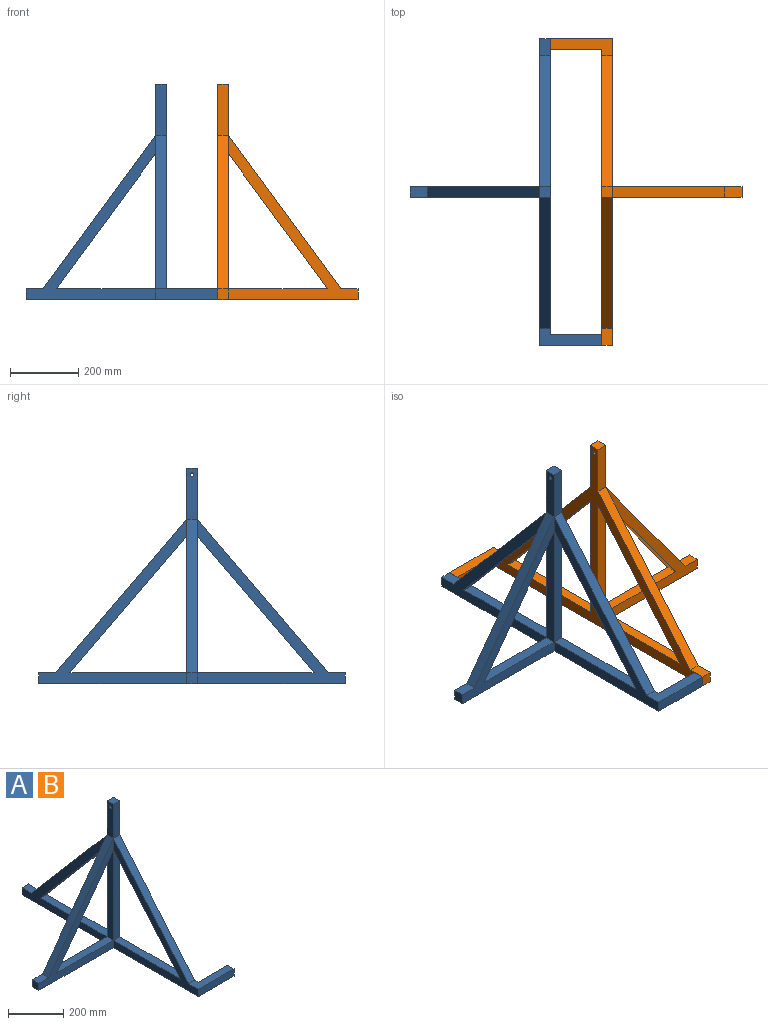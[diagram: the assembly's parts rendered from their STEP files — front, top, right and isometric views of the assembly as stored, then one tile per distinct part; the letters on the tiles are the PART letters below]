
ASSEMBLY  parts=2 mates=1
PART A: 29 faces, bbox 562x900x632 mm
  f0: plane 395.89x32mm, normal (-1,0,0), area 12668.4mm2, adj f3,f15,f16,f24
  f1: plane 482x434mm, normal (-1,0,0), area 31781.4mm2, adj f7,f10,f12,f14,f15,f18,f19
  f2: plane 150x32mm, normal (-1,0,0), area 4721.5mm2, adj f6,f8,f17,f25,f28
  f3: plane 290.32x32mm, normal (0,0,1), area 9290.2mm2, adj f0,f15,f16,f24
  f4: plane 482x434mm, normal (-1,0,0), area 31781.4mm2, adj f5,f9,f10,f13,f16,f20,f21
  f5: plane 341.93x32mm, normal (0,0,1), area 10941.8mm2, adj f4,f11,f16,f20
  f6: plane 150x32mm, normal (0,-1,0), area 4800mm2, adj f2,f11,f17,f21
  f7: plane 50x32mm, normal (0,0,1), area 1600mm2, adj f1,f11,f14,f18
  f8: plane 150x32mm, normal (0,1,0), area 4800mm2, adj f2,f11,f17,f18
  f9: plane 182x50mm, normal (0,0,1), area 6400mm2, adj f4,f11,f13,f21,f26,f27
  f10: plane 900x562mm, normal (0,0,-1), area 45760mm2, adj f1,f4,f11,f13,f14,f15,f16,f23
  f11: plane 868x632mm, normal (1,0,0), area 82684.2mm2, adj f5,f6,f7,f8,f9,f10,f12,f14
  f12: plane 341.93x32mm, normal (0,0,1), area 10941.8mm2, adj f1,f11,f15,f19
  f13: plane 182x32mm, normal (0,-1,0), area 5824mm2, adj f4,f9,f10,f27
  f14: plane 32x32mm, normal (0,1,0), area 1024mm2, adj f1,f7,f10,f11
  f15: plane 482x412mm, normal (0,1,0), area 41765.9mm2, adj f0,f1,f3,f10,f11,f12,f19,f22
  f16: plane 482x412mm, normal (0,-1,0), area 41765.9mm2, adj f0,f3,f4,f5,f10,f11,f20,f22
  f17: plane 32x32mm, normal (0,0,1), area 1024mm2, adj f2,f6,f8,f11
  f18: plane 450x384mm, normal (0,0.76,0.65), area 18930.3mm2, adj f1,f7,f8,f11
  f19: plane 400.7x341.93mm, normal (0,-0.76,-0.65), area 16856.5mm2, adj f1,f11,f12,f15
  f20: plane 400.7x341.93mm, normal (0,0.76,-0.65), area 16856.5mm2, adj f4,f5,f11,f16
  f21: plane 450x384mm, normal (0,-0.76,0.65), area 18930.3mm2, adj f4,f6,f9,f11
  f22: plane 50x32mm, normal (0,0,1), area 1600mm2, adj f15,f16,f23,f25
  f23: plane 32x32mm, normal (-1,0,0), area 1024mm2, adj f10,f15,f16,f22
  f24: plane 395.89x290.32mm, normal (0.81,0,-0.59), area 15709.7mm2, adj f0,f3,f15,f16
  f25: plane 450x330mm, normal (-0.81,0,0.59), area 17857mm2, adj f2,f15,f16,f22
  f26: plane 150x32mm, normal (0,1,0), area 4800mm2, adj f9,f10,f11,f27
  f27: plane 32x32mm, normal (1,0,0), area 1024mm2, adj f9,f10,f13,f26
  f28: cylinder r=5mm len=32mm, axis (1,0,0), area 1005.3mm2, adj f2,f11
PART B: same geometry as A
PLACE A t=(-640.56,-159.92,112.31)mm
PLACE B rot(axis=(0,0,1),180deg) t=(-490.56,-159.92,112.31)mm
MATE fastened B.f27 <-> A.f11  axis (-1,0,0) through (-640.56,290.08,128.31)mm
